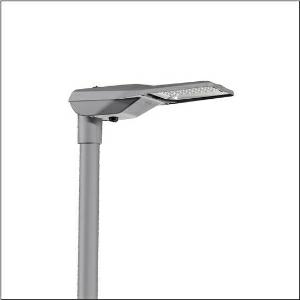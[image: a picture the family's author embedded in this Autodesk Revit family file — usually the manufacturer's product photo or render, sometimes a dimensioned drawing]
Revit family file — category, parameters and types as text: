
# Revit family: streetlight_sl_21_mini___st0_5a_5xe2b33t08jb_d15d
name_source: partatom
category: Lighting Fixtures
units: mm (PartAtom-declared; Revit-internal decimal feet)

## family parameters
Cut with Voids When Loaded = No
Host = Face
Light Source = No
Part Type = Normal
Room Calculation Point = No
Round Connector Dimension = Use Diameter
Shared = No

## types (1)
- --- (1 x LED, 12940 lm, 88.6 W, 3000K)
    Apparent Load = 89 VA
    CIE Flux Codes = 43 76 97 100 100
    Color Rendering = 70
    Color Temperature = 3000K
    Default Elevation = 1800 mm
    Description = Streetlight SL 21 mini, mast luminaire, primary light control with lens, of PMMA, primary optical cover: cover, of toughened safety glass, transparent, light distribution: ST0.5a, light emission: direct distribution, primary light characteristic: asymmetric, installation type: side-entry, post-top, LED, High Power LED, rated luminous flux: 12.940lm, luminous efficacy: 146lm/W, light colour: 730, colour temperature: 3000K, control gear: D4i, control: overheat protection, constant luminous flux control, time-dependent luminous flux control, flexible luminous flux parameterisation, pre-setting: logarithmic dimming characteristic, mains connection: 220..240V, AC, 50/60Hz, start of lifetime: 89W, end of service life: 92W, reduction: 41W, luminaire housing, of diecast aluminium, powder-coated, Siteco® metallic grey (DB 702S), corrosivity category C5 mid according to DIN EN ISO 12944, please order mast flange separately, inclination adjustable: 0°, 5°, 10°, 15°, sealing non-destructively replaceable, multi-level sealing system, length: 628mm, width: 235mm, height: 110mm, mast flange for spigot size: 42mm (side-entry): 5XC10008XM4, 60/48mm (side-entry/post-top): 5XC10108XM2, 76/60mm (side-entry/post-top): 5XC10108XM1, mounting height: 4..8m, Smart Interface below and above, protection rating (complete): IP66, insulation class (complete): insulation class II (safety insulation), certification: CE, ENEC, ENEC+, VDE, impact resistance: IK10, permissible operating ambient temperature for outdoor applications: -40..+50°C, standard-compliant lighting for roads and squares, packaging unit: 1 piece

Light Distribution: ST0.5a
    Height = 110 mm
    Lamp = 1 x LED
    Lamp Light Flux = 12940 lm
    Lamp Power = 88.6 W
    Lamp count = 1
    Length = 625 mm
    Luminous efficacy = 146 lm/W
    Manufacturer = Siteco
    ModVariant = No
    Model = 5XE2B33T08JB
    Number of Poles = 1
    OnlyDefault = Yes
    Power Factor = 1
    Product Name = Streetlight SL 21 mini | ST0.5a
    Product group = mast luminaire | pylon top
    ProductGroupID = 6100
    Protection Class = Protection class II
    Protection Degree = IP 66
    RLX_Detail_Level = 1
    RLX_Emergency_Light_Flux = 0 lm
    RLX_Emergency_Type = 0
    RLX_Emergency_Type_DB = No
    RlxData = <blob elided: 37609 chars, md5=f2e437d4>
    Socket = socket
    Standby Power = 0 W
    System Light Flux = 12940 lm
    System Power = 89 W
    Type Comments = factory setting: luminous flux: 100 % | dim-lin: 254 | 915 mA
    Type Image = l_1003514.jpg
    URL = http://relux.com
    VarID = @adj_032161
    Voltage = 0 V
    Weight = 0.00 kg
    Width = 234 mm

## geometry (parser evidence)
native form markers: Blend x4, Sweep x11
no freeform markers — native parametric forms only
